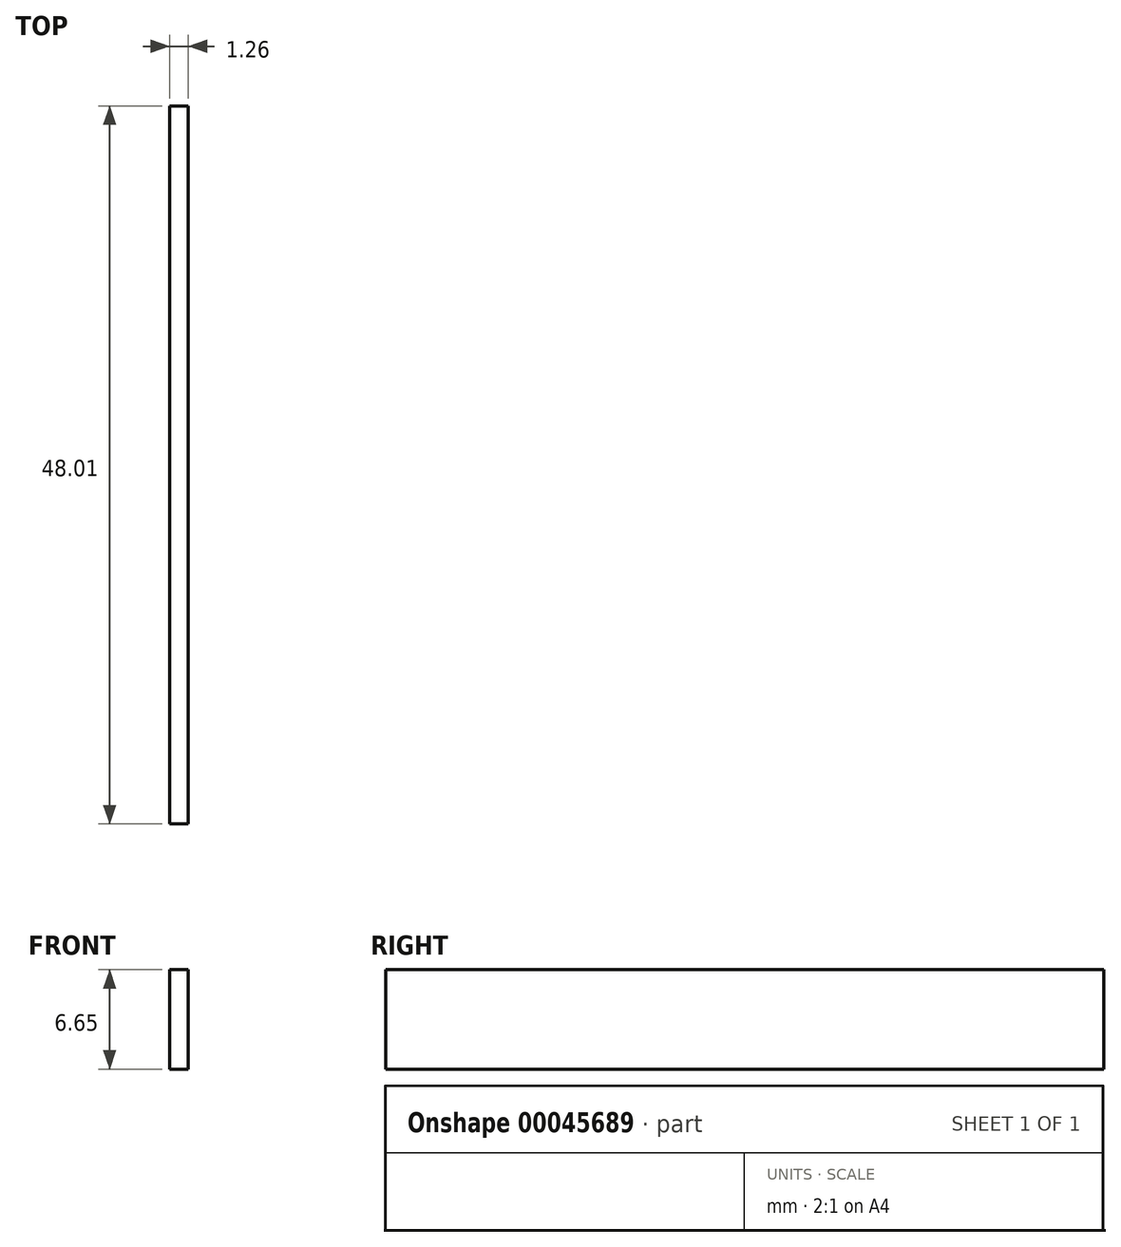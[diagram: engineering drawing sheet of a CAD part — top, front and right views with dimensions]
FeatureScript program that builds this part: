
annotation { "Feature Type Name" : "Feature", "Feature Type Description" : "" }
export const myFeature = defineFeature(function(context is Context, id is Id, definition is map)
    precondition{}
    {
        {
            var Q0;
            Q0=qCreatedBy(makeId("Right.planeOp"),FACE);
            var sketch = newSketch(context, id + "F0", { "sketchPlane" : qUnion([Q0])});
            skLineSegment(sketch, "E0", {"start": v(0, 0) * mm, "end": v(0, -6.65) * mm});
            skLineSegment(sketch, "E1", {"start": v(0, -6.65) * mm, "end": v(48, -6.65) * mm});
            skLineSegment(sketch, "E2", {"start": v(48, -6.65) * mm, "end": v(48, 0) * mm});
            skLineSegment(sketch, "E3", {"start": v(48, 0) * mm, "end": v(0, 0) * mm});
            skSolve(sketch);
        }
        {
            var Q0;
            Q0=makeQuery(id+"F0.imprint","IMPRINT",FACE,{"disambiguationData":[TD([[makeQuery(id+"F0.imprint","IMPRINT",EDGE,{"derivedFrom":sQuery(id+"F0.wireOp",EDGE,"E0")}),1.0]])]});
            extrude(context, id + "F1", {"entities" : qUnion([Q0]), "depth" : 1.26 * mm});
        }
    });
